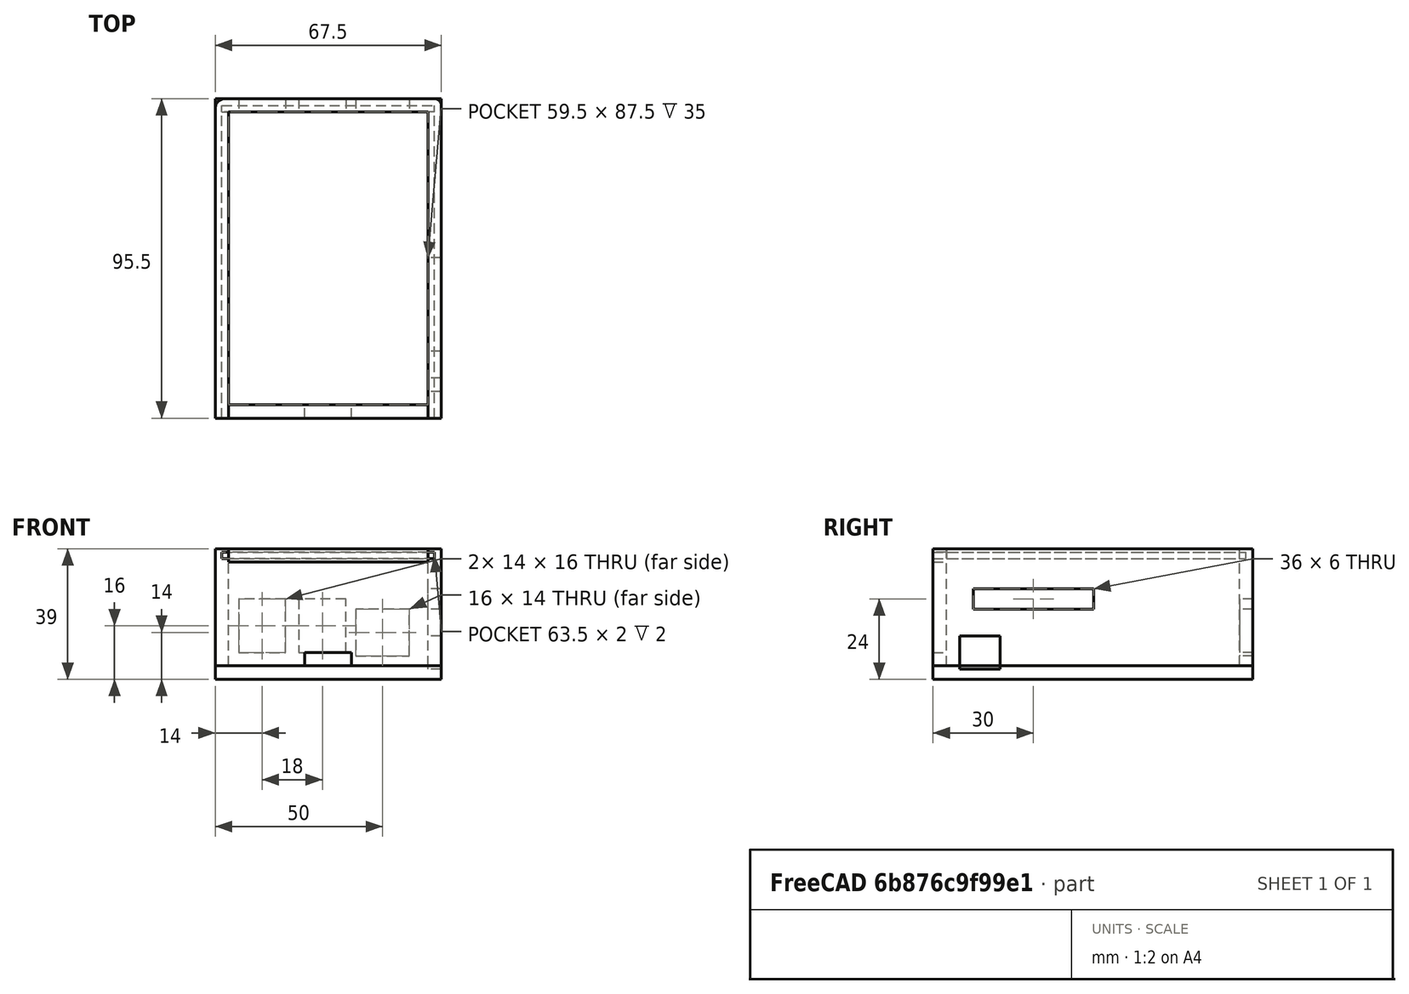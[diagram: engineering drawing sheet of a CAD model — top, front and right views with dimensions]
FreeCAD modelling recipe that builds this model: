
FCSTD DOCUMENT  (FreeCAD 0.16RUnknown)
Label: support_calaos_server
License: All rights reserved
LicenseURL: http://en.wikipedia.org/wiki/All_rights_reserved
objects: Sketcher::SketchObject×10, PartDesign::Pocket×8, PartDesign::Pad×2, PartDesign::Fillet×2, App::MeasureDistance×2, Mesh::Feature×1
note: 32 computed .brp shape members not serialized (recipe doc carries the construction recipe); baked Part::Feature solids carry a one-line shape summary decoded from their .brp

FEATURE [Sketcher::SketchObject] Sketch
  sketch-geometry (4):
    g0: LineSegment StartX=-33.75 StartY=47.75 StartZ=0 EndX=33.75 EndY=47.75 EndZ=0
    g1: LineSegment StartX=33.75 StartY=47.75 StartZ=0 EndX=33.75 EndY=-47.75 EndZ=0
    g2: LineSegment StartX=33.75 StartY=-47.75 StartZ=0 EndX=-33.75 EndY=-47.75 EndZ=0
    g3: LineSegment StartX=-33.75 StartY=-47.75 StartZ=0 EndX=-33.75 EndY=47.75 EndZ=0
  constraints (12):
    c: Coincident(g0,g1)
    c: Coincident(g1,g2)
    c: Coincident(g2,g3)
    c: Coincident(g3,g0)
    c: Horizontal(g0)
    c: Horizontal(g2)
    c: Vertical(g1)
    c: Vertical(g3)
    c: Symmetric(g0,g0,g-2)
    c: Symmetric(g0,g1,g-1)
    c: Distance(g2) = 67.5
    c: Distance(g1) = 95.5
FEATURE [PartDesign::Pad] Pad  label="base"
  Length = 4
  Length2 = 100
  Sketch = -> Sketch
  Type = 0
FEATURE [Sketcher::SketchObject] Sketch001
  ExternalGeometry = -> [Pad]
  Placement = pos=(0,0,4) rot=(0,0,1;0rad)
  Support = -> Pad [Face6]
  sketch-geometry (8):
    g0: LineSegment StartX=-29.75 StartY=43.75 StartZ=0 EndX=29.75 EndY=43.75 EndZ=0
    g1: LineSegment StartX=29.75 StartY=43.75 StartZ=0 EndX=29.75 EndY=-43.75 EndZ=0
    g2: LineSegment StartX=29.75 StartY=-43.75 StartZ=0 EndX=-29.75 EndY=-43.75 EndZ=0
    g3: LineSegment StartX=-29.75 StartY=-43.75 StartZ=0 EndX=-29.75 EndY=43.75 EndZ=0
    g4: LineSegment StartX=-33.75 StartY=47.75 StartZ=0 EndX=33.75 EndY=47.75 EndZ=0
    g5: LineSegment StartX=33.75 StartY=47.75 StartZ=0 EndX=33.75 EndY=-47.75 EndZ=0
    g6: LineSegment StartX=33.75 StartY=-47.75 StartZ=0 EndX=-33.75 EndY=-47.75 EndZ=0
    g7: LineSegment StartX=-33.75 StartY=-47.75 StartZ=0 EndX=-33.75 EndY=47.75 EndZ=0
  constraints (22):
    c: Coincident(g0,g1)
    c: Coincident(g1,g2)
    c: Coincident(g2,g3)
    c: Coincident(g3,g0)
    c: Horizontal(g0)
    c: Horizontal(g2)
    c: Vertical(g1)
    c: Vertical(g3)
    c: Symmetric(g0,g0,g-2)
    c: Symmetric(g0,g1,g-1)
    c: Distance(g2) = 59.5
    c: Distance(g1) = 87.5
    c: Coincident(g4,g5)
    c: Coincident(g5,g6)
    c: Coincident(g6,g7)
    c: Coincident(g7,g4)
    c: Horizontal(g4)
    c: Horizontal(g6)
    c: Vertical(g5)
    c: Vertical(g7)
    c: Coincident(g4,g-3)
    c: Coincident(g5,g-4)
FEATURE [PartDesign::Pad] Pad001  label="walls"
  Length = 35
  Length2 = 100
  Sketch = -> Sketch001
  Type = 0
FEATURE [Sketcher::SketchObject] Sketch002
  ExternalGeometry = -> [Pad001]
  Placement = pos=(0,-47.75,0) rot=(1,0,0;1.5708rad)
  Support = -> Pad001 [Face8]
  sketch-geometry (4):
    g0: LineSegment StartX=-7 StartY=4 StartZ=0 EndX=7 EndY=4 EndZ=0
    g1: LineSegment StartX=7 StartY=4 StartZ=0 EndX=7 EndY=8 EndZ=0
    g2: LineSegment StartX=7 StartY=8 StartZ=0 EndX=-7 EndY=8 EndZ=0
    g3: LineSegment StartX=-7 StartY=8 StartZ=0 EndX=-7 EndY=4 EndZ=0
  constraints (12):
    c: Coincident(g0,g1)
    c: Coincident(g1,g2)
    c: Coincident(g2,g3)
    c: Coincident(g3,g0)
    c: Horizontal(g0)
    c: Horizontal(g2)
    c: Vertical(g1)
    c: Vertical(g3)
    c: PointOnObject(g0,g-3)
    c: Symmetric(g1,g2,g-2)
    c: Distance(g2) = 14
    c: Distance(g3) = 4
FEATURE [PartDesign::Pocket] Pocket  label="sd_card_hole"
  Length = 0
  Sketch = -> Sketch002
  Type = 3
  UpToFace = -> Pad001 [Face12]
FEATURE [Sketcher::SketchObject] Sketch005
  ExternalGeometry = -> [Pocket]
  Placement = pos=(0,47.75,0) rot=(0,0.707107,0.707107;3.14159rad)
  Support = -> Pocket [Face6]
  sketch-geometry (4):
    g0: LineSegment StartX=-24.25 StartY=21 StartZ=0 EndX=-8.25 EndY=21 EndZ=0
    g1: LineSegment StartX=-8.25 StartY=21 StartZ=0 EndX=-8.25 EndY=7 EndZ=0
    g2: LineSegment StartX=-8.25 StartY=7 StartZ=0 EndX=-24.25 EndY=7 EndZ=0
    g3: LineSegment StartX=-24.25 StartY=7 StartZ=0 EndX=-24.25 EndY=21 EndZ=0
  constraints (12):
    c: Coincident(g0,g1)
    c: Coincident(g0,g3)
    c: Coincident(g1,g2)
    c: Coincident(g2,g3)
    c: DistanceY(g-1,g2) = 7
    c: Distance(g0) = 16
    c: Distance(g3) = 14
    c: Horizontal(g0)
    c: Horizontal(g2)
    c: Vertical(g1)
    c: Vertical(g3)
    c: DistanceX(g-3,g2) = 9.5
FEATURE [PartDesign::Pocket] Pocket003  label="ethernet_hole"
  Length = 0
  Sketch = -> Sketch005
  Type = 3
  UpToFace = -> Pocket [Face19]
FEATURE [Sketcher::SketchObject] Sketch006
  ExternalGeometry = -> [Pocket003]
  Placement = pos=(0,47.75,0) rot=(0,0.707107,0.707107;3.14159rad)
  Support = -> Pocket003 [Face6]
  sketch-geometry (8):
    g0: LineSegment StartX=-5.25 StartY=24 StartZ=0 EndX=8.75 EndY=24 EndZ=0
    g1: LineSegment StartX=8.75 StartY=24 StartZ=0 EndX=8.75 EndY=8 EndZ=0
    g2: LineSegment StartX=8.75 StartY=8 StartZ=0 EndX=-5.25 EndY=8 EndZ=0
    g3: LineSegment StartX=-5.25 StartY=8 StartZ=0 EndX=-5.25 EndY=24 EndZ=0
    g4: LineSegment StartX=12.75 StartY=24 StartZ=0 EndX=26.75 EndY=24 EndZ=0
    g5: LineSegment StartX=26.75 StartY=24 StartZ=0 EndX=26.75 EndY=8 EndZ=0
    g6: LineSegment StartX=26.75 StartY=8 StartZ=0 EndX=12.75 EndY=8 EndZ=0
    g7: LineSegment StartX=12.75 StartY=8 StartZ=0 EndX=12.75 EndY=24 EndZ=0
  constraints (24):
    c: Coincident(g0,g1)
    c: Coincident(g1,g2)
    c: Coincident(g2,g3)
    c: Coincident(g3,g0)
    c: Horizontal(g0)
    c: Horizontal(g2)
    c: Vertical(g1)
    c: Vertical(g3)
    c: Coincident(g4,g5)
    c: Coincident(g5,g6)
    c: Coincident(g6,g7)
    c: Coincident(g7,g4)
    c: Horizontal(g4)
    c: Horizontal(g6)
    c: Vertical(g5)
    c: Vertical(g7)
    c: Equal(g0,g4)
    c: Equal(g1,g5)
    c: Distance(g0) = 14
    c: Distance(g1) = 16
    c: DistanceX(g0,g4) = 4
    c: DistanceY(g0,g4) = 0
    c: DistanceY(g-3,g5) = 4
    c: DistanceX(g5,g-3) = 7
FEATURE [PartDesign::Pocket] Pocket004  label="usb_hole"
  Length = 0
  Sketch = -> Sketch006
  Type = 3
  UpToFace = -> Pocket003 [Face23]
FEATURE [Sketcher::SketchObject] Sketch010
  ExternalGeometry = -> [Pocket004]
  Placement = pos=(0,-47.75,0) rot=(1,0,0;1.5708rad)
  Support = -> Pocket004 [Face8]
  sketch-geometry (4):
    g0: LineSegment StartX=-29.75 StartY=39 StartZ=0 EndX=29.75 EndY=39 EndZ=0
    g1: LineSegment StartX=29.75 StartY=39 StartZ=0 EndX=29.75 EndY=35 EndZ=0
    g2: LineSegment StartX=29.75 StartY=35 StartZ=0 EndX=-29.75 EndY=35 EndZ=0
    g3: LineSegment StartX=-29.75 StartY=35 StartZ=0 EndX=-29.75 EndY=39 EndZ=0
  constraints (12):
    c: Horizontal(g0)
    c: Horizontal(g2)
    c: Vertical(g1)
    c: Vertical(g3)
    c: Distance(g1) = 4
    c: Symmetric(g0,g0,g-2)
    c: Coincident(g0,g3)
    c: Coincident(g2,g3)
    c: Coincident(g1,g0)
    c: Coincident(g2,g1)
    c: PointOnObject(g0,g-3)
    c: DistanceX(g-3,g0) = 4
FEATURE [PartDesign::Pocket] Pocket008  label="cover_entrance"
  Length = 4
  Sketch = -> Sketch010
  Type = 0
FEATURE [Sketcher::SketchObject] Sketch012
  ExternalGeometry = -> [Pocket008]
  Placement = pos=(0,-47.75,0) rot=(1,0,0;1.5708rad)
  Support = -> Pocket008 [Face8]
  sketch-geometry (4):
    g0: LineSegment StartX=-31.75 StartY=36 StartZ=0 EndX=31.75 EndY=36 EndZ=0
    g1: LineSegment StartX=31.75 StartY=36 StartZ=0 EndX=31.75 EndY=38 EndZ=0
    g2: LineSegment StartX=31.75 StartY=38 StartZ=0 EndX=-31.75 EndY=38 EndZ=0
    g3: LineSegment StartX=-31.75 StartY=38 StartZ=0 EndX=-31.75 EndY=36 EndZ=0
  constraints (12):
    c: Coincident(g0,g1)
    c: Coincident(g1,g2)
    c: Coincident(g2,g3)
    c: Coincident(g3,g0)
    c: Horizontal(g0)
    c: Horizontal(g2)
    c: Vertical(g1)
    c: Vertical(g3)
    c: Distance(g3) = 2
    c: Symmetric(g0,g0,g-2)
    c: DistanceY(g2,g-4) = 1
    c: DistanceX(g2,g-4) = 2
FEATURE [PartDesign::Pocket] Pocket009  label="rail_support"
  Length = 0
  Sketch = -> Sketch012
  Type = 3
  UpToFace = -> Pocket008 [Face32]
FEATURE [Sketcher::SketchObject] Sketch014
  ExternalGeometry = -> [Pocket009]
  Placement = pos=(0,43.75,0) rot=(1,0,0;1.5708rad)
  Support = -> Pocket009 [Face48]
  sketch-geometry (4):
    g0: LineSegment StartX=31.75 StartY=36 StartZ=0 EndX=-31.75 EndY=36 EndZ=0
    g1: LineSegment StartX=-31.75 StartY=36 StartZ=0 EndX=-31.75 EndY=38 EndZ=0
    g2: LineSegment StartX=-31.75 StartY=38 StartZ=0 EndX=31.75 EndY=38 EndZ=0
    g3: LineSegment StartX=31.75 StartY=38 StartZ=0 EndX=31.75 EndY=36 EndZ=0
  constraints (10):
    c: Coincident(g0,g1)
    c: Coincident(g1,g2)
    c: Coincident(g2,g3)
    c: Coincident(g3,g0)
    c: Horizontal(g0)
    c: Horizontal(g2)
    c: Vertical(g1)
    c: Vertical(g3)
    c: Coincident(g0,g-4)
    c: Coincident(g1,g-3)
FEATURE [PartDesign::Pocket] Pocket010  label="rail_support_bottom"
  Length = 2
  Sketch = -> Sketch014
  Type = 0
FEATURE [Sketcher::SketchObject] Sketch015
  ExternalGeometry = -> [Pocket010]
  Placement = pos=(33.75,0,0) rot=(0.57735,0.57735,0.57735;2.0944rad)
  Support = -> Pocket010 [Face7]
  sketch-geometry (4):
    g0: LineSegment StartX=-35.75 StartY=27 StartZ=0 EndX=0.25 EndY=27 EndZ=0
    g1: LineSegment StartX=0.25 StartY=27 StartZ=0 EndX=0.25 EndY=21 EndZ=0
    g2: LineSegment StartX=0.25 StartY=21 StartZ=0 EndX=-35.75 EndY=21 EndZ=0
    g3: LineSegment StartX=-35.75 StartY=21 StartZ=0 EndX=-35.75 EndY=27 EndZ=0
  constraints (12):
    c: Coincident(g0,g1)
    c: Coincident(g1,g2)
    c: Coincident(g2,g3)
    c: Coincident(g3,g0)
    c: Horizontal(g0)
    c: Horizontal(g2)
    c: Vertical(g1)
    c: Vertical(g3)
    c: DistanceY(g-1,g1) = 21
    c: Distance(g1) = 6
    c: Distance(g2) = 36
    c: DistanceX(g-3,g2) = 12
FEATURE [PartDesign::Pocket] Pocket011  label="terminal_block_hole"
  Length = 0
  Sketch = -> Sketch015
  Type = 3
  UpToFace = -> Pocket010 [Face48]
FEATURE [Sketcher::SketchObject] Sketch016
  ExternalGeometry = -> [Pocket011]
  Placement = pos=(33.75,0,0) rot=(0.57735,0.57735,0.57735;2.0944rad)
  Support = -> Pocket011 [Face7]
  sketch-geometry (4):
    g0: LineSegment StartX=-27.75 StartY=3 StartZ=0 EndX=-39.75 EndY=3 EndZ=0
    g1: LineSegment StartX=-39.75 StartY=3 StartZ=0 EndX=-39.75 EndY=13 EndZ=0
    g2: LineSegment StartX=-39.75 StartY=13 StartZ=0 EndX=-27.75 EndY=13 EndZ=0
    g3: LineSegment StartX=-27.75 StartY=13 StartZ=0 EndX=-27.75 EndY=3 EndZ=0
  constraints (12):
    c: Coincident(g0,g1)
    c: Coincident(g1,g2)
    c: Coincident(g2,g3)
    c: Coincident(g3,g0)
    c: Horizontal(g0)
    c: Horizontal(g2)
    c: Vertical(g1)
    c: Vertical(g3)
    c: Distance(g0) = 12
    c: Distance(g1) = 10
    c: DistanceY(g0,g-3) = 1
    c: DistanceX(g-3,g0) = 8
FEATURE [PartDesign::Pocket] Pocket012  label="micro_usb_hole"
  Length = 0
  Sketch = -> Sketch016
  Type = 3
  UpToFace = -> Pocket011 [Face47]
FEATURE [PartDesign::Fillet] Fillet
  Base = -> Pocket012 [Edge21]
  Radius = 2
FEATURE [PartDesign::Fillet] Fillet001
  Base = -> Fillet [Edge23]
  Radius = 3
FEATURE [App::MeasureDistance] Distance  label="Distance: 59,5 mm"
  Distance = 59.5
  P1 = (-29.75,-47.75,35)
  P2 = (29.75,-47.75,35)
FEATURE [App::MeasureDistance] Distance001  label="Distance: 91,5055 mm"
  Distance = 91.5055
  P1 = (29.6887,43.75,36)
  P2 = (29.7019,-47.75,35)
FEATURE [Mesh::Feature] cover_calaos_server
  Placement = pos=(0,-1,36.3) rot=(0,0,1;0rad)
